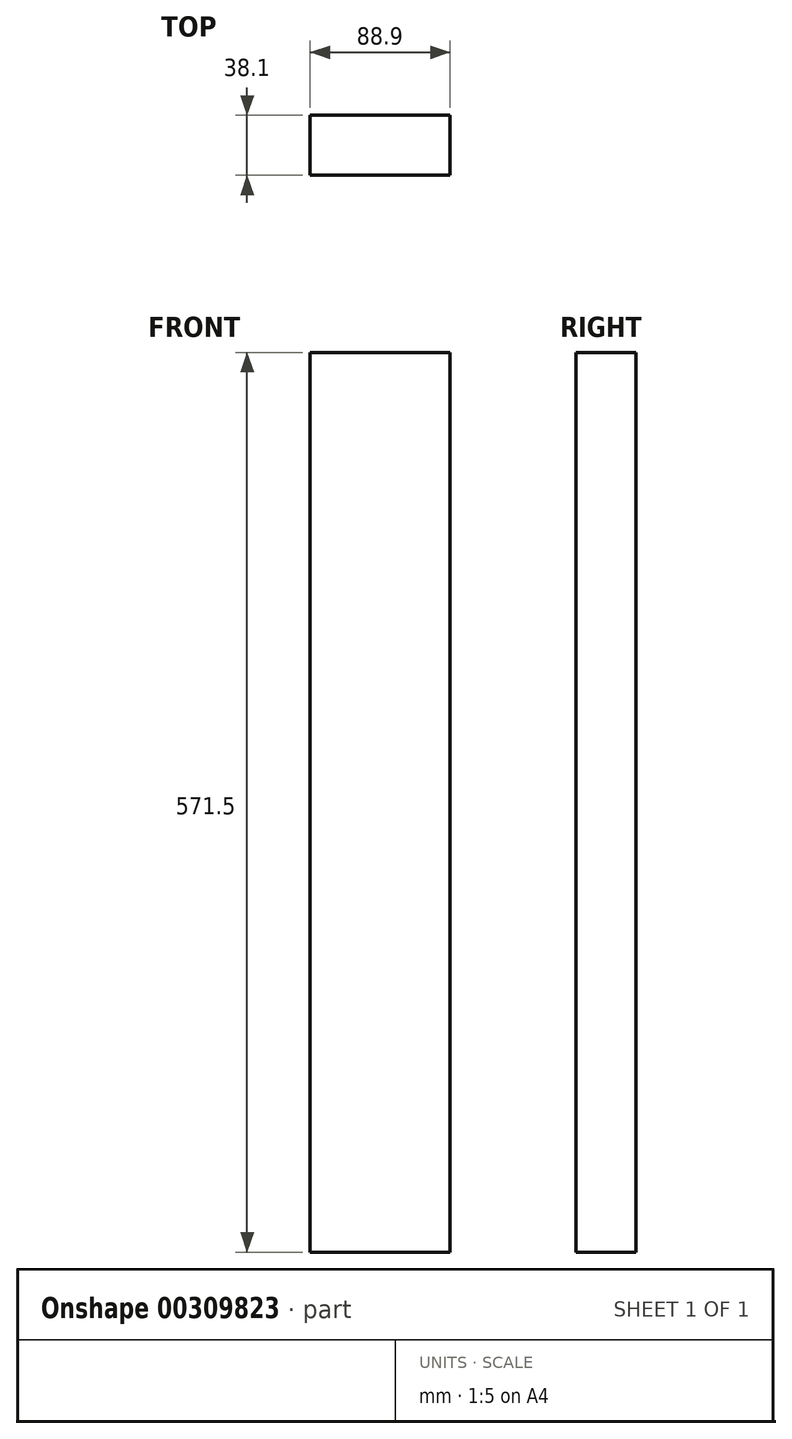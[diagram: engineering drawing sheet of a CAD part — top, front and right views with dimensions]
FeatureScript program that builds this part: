
annotation { "Feature Type Name" : "Feature", "Feature Type Description" : "" }
export const myFeature = defineFeature(function(context is Context, id is Id, definition is map)
    precondition{}
    {
        {
            var Q0;
            Q0=qCreatedBy(makeId("Front.planeOp"),FACE);
            var sketch = newSketch(context, id + "F0", { "sketchPlane" : qUnion([Q0])});
            skLineSegment(sketch, "E0.bottom", {"start": v(44.45, 285.75) * mm, "end": v(-44.45, 285.75) * mm});
            skLineSegment(sketch, "E0.top", {"start": v(44.45, -285.75) * mm, "end": v(-44.45, -285.75) * mm});
            skLineSegment(sketch, "E0.left", {"start": v(44.45, 285.75) * mm, "end": v(44.45, -285.75) * mm});
            skLineSegment(sketch, "E0.right", {"start": v(-44.45, 285.75) * mm, "end": v(-44.45, -285.75) * mm});
            skPoint(sketch, "E0.middle", {"position": v(0, 0) * mm});
            skSolve(sketch);
        }
        {
            var Q0;
            Q0=qSketchRegion(id+"F0",true);
            extrude(context, id + "F1", {"entities" : qUnion([Q0]), "depth" : 38.1 * mm});
        }
    });
